# Revit family: Power-ModularDevices-GEWISS-90AM-RELASES_MPS
name_source: partatom
category: Apparecchi elettrici
revit_build: Autodesk Revit 2016 (Build: 20161004_0715(x64)
units: mm (PartAtom-declared; Revit-internal decimal feet)

## family parameters
Condiviso = No
Host = Superficie
Mantenere orientamento annotazione = Sì
Numero OmniClass = 23.80.50.00
Punto di calcolo locali = Sì
Quota connettore circolare = Usa diametro
Taglio con vuoti quando caricato = No
Tipo di parte = Normale
Titolo OmniClass = Terminals for Power Supply

## types (3) — shared parameters
Catalogue = POWER
Catalogue Range = 90 AM
Electrocod = 140
IDF = 0853d5eb-5065-40ff-990a-670f492df11c
IDT = b0d06194-5e63-4575-adf9-f55bbd5faea3
Immagine tipo = GW96770.jpg
No. Chorus modules = 1
No. of modules EN 50022 = 1
Numero di poli = 1
Produttore = GEWISS S.p.A.
Prospetto di default = 1219 mm
SEO = Release
Spostamento_x = -340 mm
Technical sheet = https://www.gewiss.com
URL = https://www.gewiss.com
Version file RFA = 18.0
carico = Altro
potenza in watt = 0 V

## per-type parameters (varying)
| type | Descrizione | EAN code | Modello | Rated voltage | Rated voltage (V) |
| GW96769 - UNDER VOLTAGE RELEASES MPS 230V | UNDER VOLTAGE RELEASES MPS 230V | 8011564189904 | GW96769 | 230Vac | 230 ac |
| GW96770 - UNDER VOLTAGE RELEASES MPS 400V | UNDER VOLTAGE RELEASES MPS 400V | 8011564189911 | GW96770 | 400Vac | 400 ac |
| GW96767 - SHUNT TRIP RELEASES MPS 110-415 V | SHUNT TRIP RELEASES MPS 110-415 V | 8011564189881 | GW96767 | 110-415Vac | 110-415 ac |
